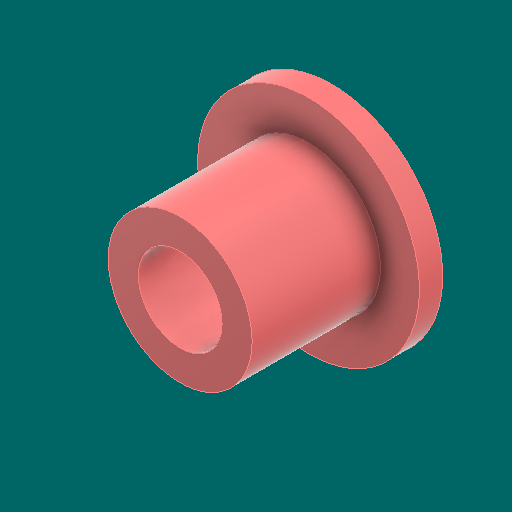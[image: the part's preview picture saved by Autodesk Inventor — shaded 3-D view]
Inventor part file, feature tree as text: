
AUTODESK INVENTOR PART (.ipt)
format: ipt  version: 2023.1 (Build 271208000, 208)  size: 310,272 bytes
history: native  units: in
note: dims shown in document units (in); Inventor stores cm internally (conversion verified against a paired STEP export)
features: extrude x2, sketch x2, chamfer x1
ambient origin geometry x8: Origin, YZ Plane, XZ Plane, XY Plane, X Axis, Y Axis, Z Axis, Center Point
bodies: Solid1 (feature_tree)
feature tree (5):
  extrude  "Extrusion1"  Depth=0.18in
  extrude  "Extrusion2"  Depth=0.05in
  chamfer  "Chamfer1"  Distance=0.05in
  sketch  "Sketch1"  dims[d0=0.3091in d1=0.18in]
  sketch  "Sketch2"  dims[d2=0.2756in d3=0.0in d4=0.4764in d5=0.05in d6=0.0in d7=0.0236in d8=0.125in d9=45.0deg]
